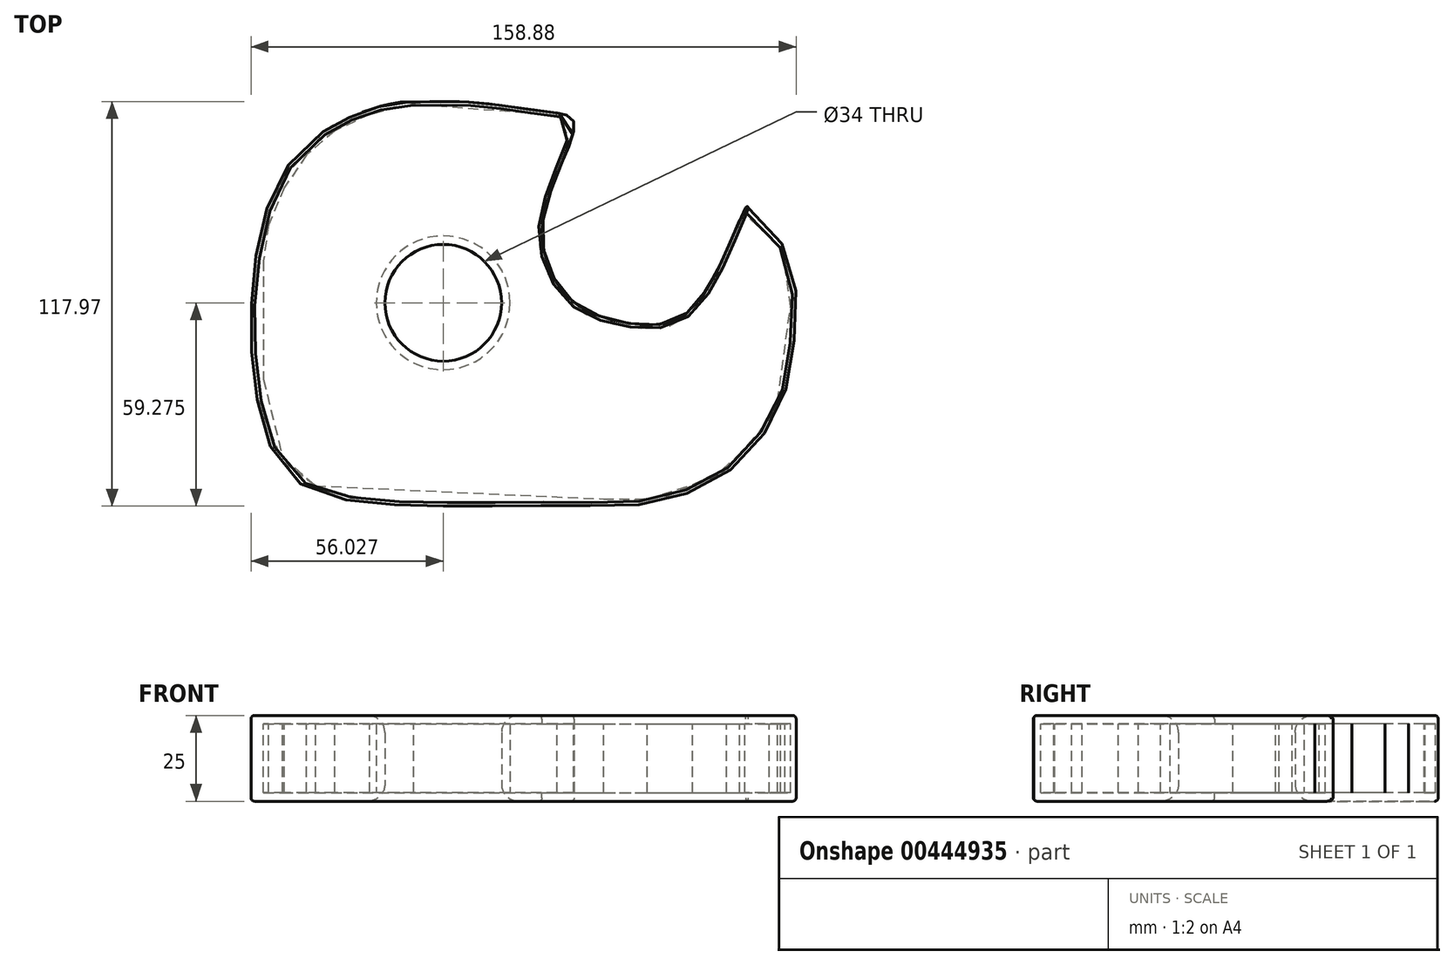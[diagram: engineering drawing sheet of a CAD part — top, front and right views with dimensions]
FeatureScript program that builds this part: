
annotation { "Feature Type Name" : "Feature", "Feature Type Description" : "" }
export const myFeature = defineFeature(function(context is Context, id is Id, definition is map)
    precondition{}
    {
        {
            var Q0;
            Q0=qCreatedBy(makeId("Top.planeOp"),FACE);
            var sketch = newSketch(context, id + "F0", { "sketchPlane" : qUnion([Q0])});
            skFitSpline(sketch, "E0", {"points": [v(35.21, 13.06) * mm, v(13.45, 21.77) * mm, v(4.75, 43.76) * mm, v(4.29, 82.93) * mm, v(19.35, 117.44) * mm, v(44.95, 129.39) * mm, v(50.64, 129.67) * mm, v(66.57, 129.67) * mm, v(89.33, 126.83) * mm, v(97, 124.27) * mm, v(93.6, 111.75) * mm, v(89.04, 99.23) * mm, v(87.9, 92.98) * mm, v(89.04, 83.87) * mm, v(97, 71.36) * mm, v(113.8, 65.1) * mm, v(132.85, 70.79) * mm, v(147.64, 99.23) * mm, v(148.5, 97.53) * mm, v(151.91, 94.68) * mm, v(160.73, 81.6) * mm, v(159.3, 47.46) * mm, v(155.6, 37.22) * mm, v(148.04, 27.64) * mm, v(139.2, 19.87) * mm, v(119.78, 12.8) * mm, v(95.4, 12.1) * mm, v(35.21, 13.06) * mm]});
            skCircle(sketch, "E1", {"center": v(59.09, 71.15) * mm, "radius": 15 * mm});
            skCircle(sketch, "E2", {"center": v(59.09, 71.15) * mm, "radius": 17 * mm});
            skSolve(sketch);
        }
        {
            var Q0;
            Q0=makeQuery(id+"F0.imprint","IMPRINT",FACE,{"disambiguationData":[TD([[makeQuery(id+"F0.imprint","IMPRINT",EDGE,{"derivedFrom":sQuery(id+"F0.wireOp",EDGE,"E0")}),-1.0]])]});
            extrude(context, id + "F1", {"entities" : qUnion([Q0]), "depth" : 25 * mm});
        }
        {
            var Q0;
            Q0=makeQuery(id+"F1.opExtrude","SWEPT_FACE",FACE,{"disambiguationData":[OSD([sQuery(id+"F0.wireOp",EDGE,"E0")])]});
            shell(context, id + "F2", {"entities" : qUnion([Q0]), "thickness" : 2.5 * mm});
        }
        {
            var Q0;
            Q0=makeQuery(id+"F1.opExtrude","CAP_EDGE",EDGE,{"disambiguationData":[OSD([sQuery(id+"F0.wireOp",EDGE,"E2")])],"isStart":false});
            fillet(context, id + "F3", {"entities" : qUnion([Q0]), "radius" : 5 * mm, "tangentPropagation" : true, "allowEdgeOverflow" : false});
        }
        {
            var Q0;
            Q0=makeQuery(id+"F1.opExtrude","CAP_EDGE",EDGE,{"disambiguationData":[OSD([sQuery(id+"F0.wireOp",EDGE,"E2")])],"isStart":true});
            fillet(context, id + "F4", {"entities" : qUnion([Q0]), "radius" : 5 * mm, "tangentPropagation" : true, "allowEdgeOverflow" : false});
        }
        {
            var Q0;
            Q0=makeQuery(id+"F1.opExtrude","CAP_EDGE",EDGE,{"disambiguationData":[OSD([sQuery(id+"F0.wireOp",EDGE,"E0")])],"isStart":false});
            fillet(context, id + "F5", {"entities" : qUnion([Q0]), "radius" : 1 * mm, "tangentPropagation" : true, "allowEdgeOverflow" : false});
        }
        {
            var Q0;
            Q0=makeQuery(id+"F1.opExtrude","CAP_EDGE",EDGE,{"disambiguationData":[OSD([sQuery(id+"F0.wireOp",EDGE,"E0")])],"isStart":true});
            fillet(context, id + "F6", {"entities" : qUnion([Q0]), "radius" : 1 * mm, "tangentPropagation" : true, "allowEdgeOverflow" : false});
        }
        {
            var Q0;
            {var subQ0=sQuery(id+"F0.wireOp",EDGE,"E2");var subQ1=sQuery(id+"F0.wireOp",EDGE,"E0");Q0=makeQuery(id+"F2.opShell","OFFSET_FACE",FACE,{"disambiguationData":[OSD([subQ1,subQ0]),TDD([makeQuery(id+"F1.opExtrude","CAP_FACE",FACE,{"disambiguationData":[OSD([subQ1,subQ0])],"isStart":false})])]});}
            var sketch = newSketch(context, id + "F7", { "sketchPlane" : qUnion([Q0])});
            skLineSegment(sketch, "E3", {"start": v(92.24, -125.75) * mm, "end": v(50.48, -129.04) * mm});
            skLineSegment(sketch, "E4", {"start": v(50.48, -129.04) * mm, "end": v(37.64, -126.06) * mm});
            skLineSegment(sketch, "E5", {"start": v(37.64, -126.06) * mm, "end": v(27.46, -121.33) * mm});
            skLineSegment(sketch, "E6", {"start": v(27.46, -121.33) * mm, "end": v(19.27, -114.28) * mm});
            skLineSegment(sketch, "E7", {"start": v(19.27, -114.28) * mm, "end": v(12.79, -104.75) * mm});
            skLineSegment(sketch, "E8", {"start": v(12.79, -104.75) * mm, "end": v(8.15, -93.87) * mm});
            skLineSegment(sketch, "E9", {"start": v(8.15, -93.87) * mm, "end": v(6.7, -83.43) * mm});
            skLineSegment(sketch, "E10", {"start": v(6.7, -83.43) * mm, "end": v(6.7, -48.89) * mm});
            skLineSegment(sketch, "E11", {"start": v(6.7, -48.89) * mm, "end": v(12.28, -26.06) * mm});
            skLineSegment(sketch, "E12", {"start": v(12.28, -26.06) * mm, "end": v(21.88, -17.8) * mm});
            skLineSegment(sketch, "E13", {"start": v(21.88, -17.8) * mm, "end": v(105.8, -13.97) * mm});
            skLineSegment(sketch, "E14", {"start": v(105.8, -13.97) * mm, "end": v(118.6, -13.97) * mm});
            skLineSegment(sketch, "E15", {"start": v(118.6, -13.97) * mm, "end": v(131.7, -18.13) * mm});
            skLineSegment(sketch, "E16", {"start": v(131.7, -18.13) * mm, "end": v(141.6, -22.98) * mm});
            skLineSegment(sketch, "E17", {"start": v(141.6, -22.98) * mm, "end": v(154.1, -36.64) * mm});
            skLineSegment(sketch, "E18", {"start": v(154.1, -36.64) * mm, "end": v(156.48, -42.4) * mm});
            skLineSegment(sketch, "E19", {"start": v(156.48, -42.4) * mm, "end": v(160.3, -70.02) * mm});
            skLineSegment(sketch, "E20", {"start": v(160.3, -70.02) * mm, "end": v(158.66, -82.44) * mm});
            skLineSegment(sketch, "E21", {"start": v(158.66, -82.44) * mm, "end": v(157.47, -87.33) * mm});
            skLineSegment(sketch, "E22", {"start": v(157.47, -87.33) * mm, "end": v(148.03, -95.97) * mm});
            skLineSegment(sketch, "E23", {"start": v(148.03, -95.97) * mm, "end": v(147.01, -96.9) * mm});
            skLineSegment(sketch, "E24", {"start": v(97.06, -121.2) * mm, "end": v(92.24, -125.75) * mm});
            skLineSegment(sketch, "E25", {"start": v(97.06, -121.2) * mm, "end": v(94.26, -118.24) * mm});
            skLineSegment(sketch, "E26", {"start": v(94.26, -118.24) * mm, "end": v(46.77, -124.95) * mm});
            skLineSegment(sketch, "E27", {"start": v(46.77, -124.95) * mm, "end": v(32.87, -121.2) * mm});
            skLineSegment(sketch, "E28", {"start": v(32.87, -121.2) * mm, "end": v(21.85, -109.51) * mm});
            skPoint(sketch, "E28.endSnap0", {"position": v(16.03, -109.51) * mm});
            skLineSegment(sketch, "E29", {"start": v(21.85, -109.51) * mm, "end": v(13.98, -92.99) * mm});
            skLineSegment(sketch, "E30", {"start": v(13.98, -92.99) * mm, "end": v(11.83, -65.69) * mm});
            skLineSegment(sketch, "E31", {"start": v(11.83, -65.69) * mm, "end": v(10.06, -43.24) * mm});
            skLineSegment(sketch, "E32", {"start": v(10.06, -43.24) * mm, "end": v(18.5, -26.15) * mm});
            skLineSegment(sketch, "E33", {"start": v(18.5, -26.15) * mm, "end": v(27.96, -19.72) * mm});
            skLineSegment(sketch, "E34", {"start": v(27.96, -19.72) * mm, "end": v(118.6, -17.56) * mm});
            skLineSegment(sketch, "E35", {"start": v(118.6, -17.56) * mm, "end": v(136.65, -25.52) * mm});
            skPoint(sketch, "E35.endSnap0", {"position": v(136.65, -20.55) * mm});
            skLineSegment(sketch, "E36", {"start": v(136.65, -25.52) * mm, "end": v(153.53, -43.42) * mm});
            skLineSegment(sketch, "E37", {"start": v(153.53, -43.42) * mm, "end": v(155.65, -70.33) * mm});
            skLineSegment(sketch, "E38", {"start": v(155.65, -70.33) * mm, "end": v(156.76, -84.32) * mm});
            skLineSegment(sketch, "E39", {"start": v(156.76, -84.32) * mm, "end": v(146.77, -93.74) * mm});
            skLineSegment(sketch, "E40", {"start": v(146.77, -93.74) * mm, "end": v(147.01, -96.9) * mm});
            skLineSegment(sketch, "E41", {"start": v(97.06, -121.2) * mm, "end": v(101.22, -117.29) * mm});
            skLineSegment(sketch, "E42", {"start": v(101.22, -117.29) * mm, "end": v(92.72, -94.48) * mm});
            skLineSegment(sketch, "E43", {"start": v(92.72, -94.48) * mm, "end": v(105.12, -70.63) * mm});
            skLineSegment(sketch, "E44", {"start": v(105.12, -70.63) * mm, "end": v(127.5, -75.38) * mm});
            skLineSegment(sketch, "E45", {"start": v(127.5, -75.38) * mm, "end": v(147.01, -96.9) * mm});
            skSolve(sketch);
        }
        {
            var Q0;
            Q0=makeQuery(id+"F7.imprint","IMPRINT",FACE,{"disambiguationData":[TD([[makeQuery(id+"F7.imprint","IMPRINT",EDGE,{"derivedFrom":sQuery(id+"F7.wireOp",EDGE,"E3")}),1.0]])]});
            extrude(context, id + "F8", {"entities" : qUnion([Q0]), "operationType" : NewBodyOperationType.ADD, "depth" : 20 * mm});
        }
    });
